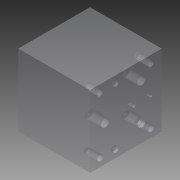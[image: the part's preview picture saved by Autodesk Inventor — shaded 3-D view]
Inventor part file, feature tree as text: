
AUTODESK INVENTOR PART (.ipt)
format: ipt  version: 2014 (Build 180170000, 170)  size: 226,816 bytes
history: native  units: mm
features: other x48, extrude x20, sketch x20
ambient origin geometry x8: Origin, YZ Plane, XZ Plane, XY Plane, X Axis, Y Axis, Z Axis, Center Point
bodies: 实体1 (feature_tree)
feature tree (88):
  extrude  "拉伸1"  Depth=235.0mm
  other  "UCS1"
  other  "UCS2"
  other  "UCS3"
  other  "UCS4"
  other  "UCS5"
  other  "UCS6"
  extrude  "拉伸2"  Depth=124.0mm
  extrude  "拉伸3"  Depth=17.0mm
  extrude  "拉伸4"  Depth=88.9mm
  extrude  "拉伸5"  TaperAngle=0.0deg  [1 undecoded]
  extrude  "拉伸6"  Depth=177.8mm
  extrude  "拉伸7"  Depth=177.8mm
  extrude  "拉伸8"  Depth=50.0mm
  extrude  "拉伸9"  Depth=50.0mm
  extrude  "拉伸10"  Depth=20.0mm
  extrude  "拉伸11"  Depth=40.0mm
  extrude  "拉伸12"  Depth=17.5mm
  extrude  "拉伸13"  Depth=56.8mm
  extrude  "拉伸14"  Depth=144.5mm
  extrude  "拉伸15"  Depth=34.9mm
  extrude  "拉伸16"  Depth=55.8mm TaperAngle=0.0deg
  extrude  "拉伸17"  Depth=56.8mm
  extrude  "拉伸18"  Depth=28.4mm
  extrude  "拉伸19"  Depth=144.5mm
  extrude  "拉伸20"  Depth=161.9mm
  sketch  "草图1"  dims[d0=250.0mm d1=0.0mm]
  sketch  "草图2"  dims[d2=0.0mm d3=0.0mm d4=0.0mm d5=0.0mm d6=0.0mm d7=0.0mm]
  sketch  "草图3"  dims[d8=0.0mm d9=0.0mm d10=0.0mm d11=0.0mm d12=0.0mm d13=0.0mm]
  sketch  "草图4"  dims[d14=0.0mm d15=0.0mm d16=0.0mm d17=0.0mm d18=0.0mm d19=0.0mm]
  sketch  "草图5"  dims[d20=0.0mm d21=0.0mm d22=0.0mm d23=0.0mm d24=0.0mm d25=0.0mm]
  sketch  "草图6"  dims[d26=0.0mm d27=0.0mm d28=0.0mm d29=0.0mm d30=0.0mm d31=0.0mm]
  sketch  "草图7"  dims[d32=0.0mm d33=0.0mm d34=0.0mm d35=0.0mm d36=0.0mm d37=0.0mm d38=235.0mm]
  sketch  "草图8"  dims[d39=216.0mm d40=124.0mm]
  sketch  "草图9"  dims[d41=125.0mm d42=17.0mm]
  sketch  "草图10"  dims[d43=98.4mm d44=88.9mm]
  sketch  "草图11"  dims[d45=196.8mm d46=0.0mm]
  sketch  "草图12"  dims[d47=196.8mm d48=177.8mm]
  sketch  "草图13"  dims[d49=0.0mm d50=177.8mm]
  sketch  "草图14"  dims[d51=50.0mm d52=0.0mm d53=50.0mm d54=-10.297443mm]
  sketch  "草图15"  dims[d55=50.0mm d56=-10.297443mm d57=50.0mm d58=-10.297443mm]
  sketch  "草图16"  dims[d59=50.0mm d60=-10.297443mm d61=20.0mm]
  sketch  "草图17"  dims[d62=40.0mm d63=0.0mm d64=28.4mm]
  sketch  "草图18"  dims[d65=98.4mm d66=17.5mm]
  sketch  "草图19"  dims[d67=56.8mm d68=0.0mm d69=56.8mm d70=-10.297443mm]
  sketch  "草图20"  dims[d71=28.4mm d72=144.5mm d73=34.9mm d74=55.8mm d75=0.0mm d76=56.8mm d77=-10.297443mm d78=28.4mm d79=144.5mm d80=161.9mm d81=54.8mm d82=0.0mm d83=54.8mm d84=-10.297443mm d85=11.1mm d86=98.4mm d87=119.0mm d88=22.2mm d89=0.0mm d90=22.2mm d91=-10.297443mm d92=7.9mm d93=98.4mm d94=177.8mm d95=15.8mm d96=0.0mm d97=15.8mm d98=-10.297443mm d99=19.8mm d100=1.6mm d101=55.5mm d102=198.5mm d103=55.5mm d104=8.0mm d105=0.0mm d106=8.0mm d107=-10.297443mm d108=8.0mm d109=-10.297443mm]
  other  "UCS1: YZ 平面"
  other  "UCS1: XZ 平面"
  other  "UCS1: XY 平面"
  other  "UCS1: X 轴"
  other  "UCS1: Y 轴"
  other  "UCS1: Z 轴"
  other  "UCS1: 原点"
  other  "UCS2: YZ 平面"
  other  "UCS2: XZ 平面"
  other  "UCS2: XY 平面"
  other  "UCS2: X 轴"
  other  "UCS2: Y 轴"
  other  "UCS2: Z 轴"
  other  "UCS2: 原点"
  other  "UCS3: YZ 平面"
  other  "UCS3: XZ 平面"
  other  "UCS3: XY 平面"
  other  "UCS3: X 轴"
  other  "UCS3: Y 轴"
  other  "UCS3: Z 轴"
  other  "UCS3: 原点"
  other  "UCS4: YZ 平面"
  other  "UCS4: XZ 平面"
  other  "UCS4: XY 平面"
  other  "UCS4: X 轴"
  other  "UCS4: Y 轴"
  other  "UCS4: Z 轴"
  other  "UCS4: 原点"
  other  "UCS5: YZ 平面"
  other  "UCS5: XZ 平面"
  other  "UCS5: XY 平面"
  other  "UCS5: X 轴"
  other  "UCS5: Y 轴"
  other  "UCS5: Z 轴"
  other  "UCS5: 原点"
  other  "UCS6: YZ 平面"
  other  "UCS6: XZ 平面"
  other  "UCS6: XY 平面"
  other  "UCS6: X 轴"
  other  "UCS6: Y 轴"
  other  "UCS6: Z 轴"
  other  "UCS6: 原点"
note: 1 required parameter value undecoded (feature->parameter linkage not recoverable at this tier; creation-order binding heuristic only, values carry confidence <= 0.55)
